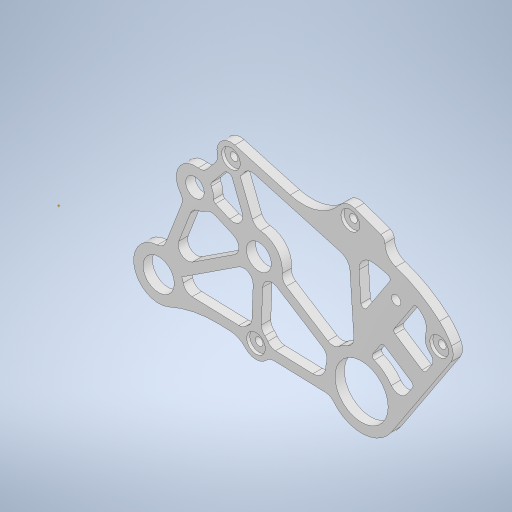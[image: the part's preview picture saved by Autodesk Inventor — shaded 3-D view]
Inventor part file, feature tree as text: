
AUTODESK INVENTOR PART (.ipt)
format: ipt  version: 2023.1 (Build 271208000, 208)  size: 794,624 bytes
history: native  units: mm
features: extrude x2, sketch x1, fillet x1
ambient origin geometry x8: Origin, YZ Plane, XZ Plane, XY Plane, X Axis, Y Axis, Z Axis, Center Point
bodies: Solid2 (feature_tree)
feature tree (4):
  sketch  "Sketch4"  dims[d238=3.0mm d239=0.0mm d438=2.0mm d439=0.0mm d522=2.5mm d523=6.0mm d524=10.05mm d525=2.5mm d526=15.0mm d527=2.5mm d528=9.0mm d529=9.0mm d530=3.0mm d531=17.05mm d532=2.5mm d533=9.0mm d534=3.0mm d535=3.0mm d536=3.0mm d537=3.0mm d538=3.0mm d539=1.5mm d540=1.5mm d541=3.0mm d542=1.5mm d543=3.0mm d544=3.0mm d545=1.5mm d546=3.0mm d547=1.5mm d548=3.0mm d549=1.5mm d550=3.0mm d551=3.0mm d552=1.5mm d553=2.0mm d554=3.0mm d555=1.5mm d556=3.0mm d557=3.0mm d558=6.05mm d559=6.05mm d560=6.05mm d561=3.0mm d562=4.0mm d563=3.0mm d564=15.0mm d565=2.0mm d566=3.0mm d567=4.0mm d568=18.0mm d569=2.0mm d570=3.0mm d571=3.0mm d572=3.0mm d573=3.0mm d574=3.0mm d575=3.0mm d576=3.0mm d577=3.0mm d578=3.0mm d579=3.0mm d580=3.0mm d581=3.0mm d582=3.0mm d583=3.0mm d584=3.0mm d585=4.0mm d586=3.0mm d587=3.0mm d588=3.0mm d589=3.0mm d590=1.0mm d591=1.0mm d592=4.0mm d593=4.0mm d594=1.0mm d595=1.0mm d596=1.0mm d597=1.0mm d598=3.0mm d599=18.522635mm d600=9.261317mm d601=6.05mm d602=36.0mm d603=7.0mm d604=3.0mm d605=3.0mm d606=3.0mm d607=3.0mm d608=6.108652mm d609=15.0mm d610=12.0mm d611=8.05mm d612=1.0mm]
  extrude  "Extrusion3"  Depth=2.0mm TaperAngle=0.0deg
  extrude  "押し出し6"  Depth=1.0mm
  fillet  "フィレット5"  Radius=1.0mm
